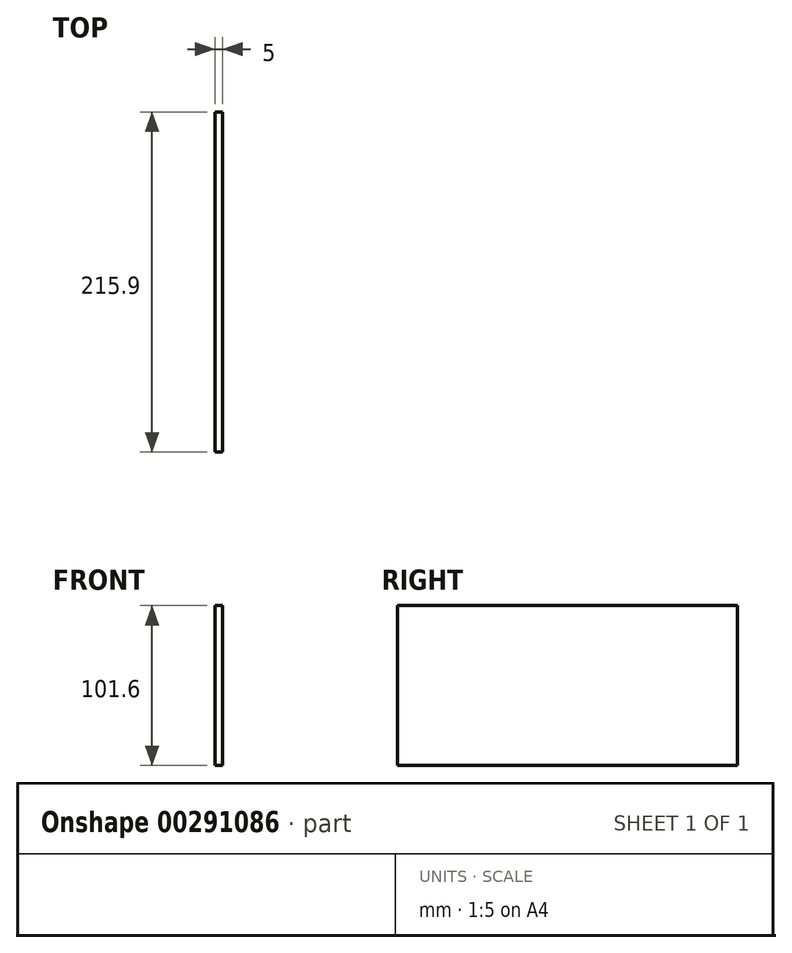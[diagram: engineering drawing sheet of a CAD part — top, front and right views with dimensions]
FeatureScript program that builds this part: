
annotation { "Feature Type Name" : "Feature", "Feature Type Description" : "" }
export const myFeature = defineFeature(function(context is Context, id is Id, definition is map)
    precondition{}
    {
        {
            var Q0;
            Q0=qCreatedBy(makeId("Right.planeOp"),FACE);
            var sketch = newSketch(context, id + "F0", { "sketchPlane" : qUnion([Q0])});
            skLineSegment(sketch, "E0.bottom", {"start": v(0, 0) * mm, "end": v(215.9, 0) * mm});
            skLineSegment(sketch, "E0.top", {"start": v(0, 101.6) * mm, "end": v(215.9, 101.6) * mm});
            skLineSegment(sketch, "E0.left", {"start": v(0, 0) * mm, "end": v(0, 101.6) * mm});
            skLineSegment(sketch, "E0.right", {"start": v(215.9, 0) * mm, "end": v(215.9, 101.6) * mm});
            skSolve(sketch);
        }
        {
            var Q0;
            Q0 = qSketchRegion(id + "F0", true);
            extrude(context, id + "F1", {"entities" : qUnion([Q0]), "depth" : 5 * mm});
        }
    });
